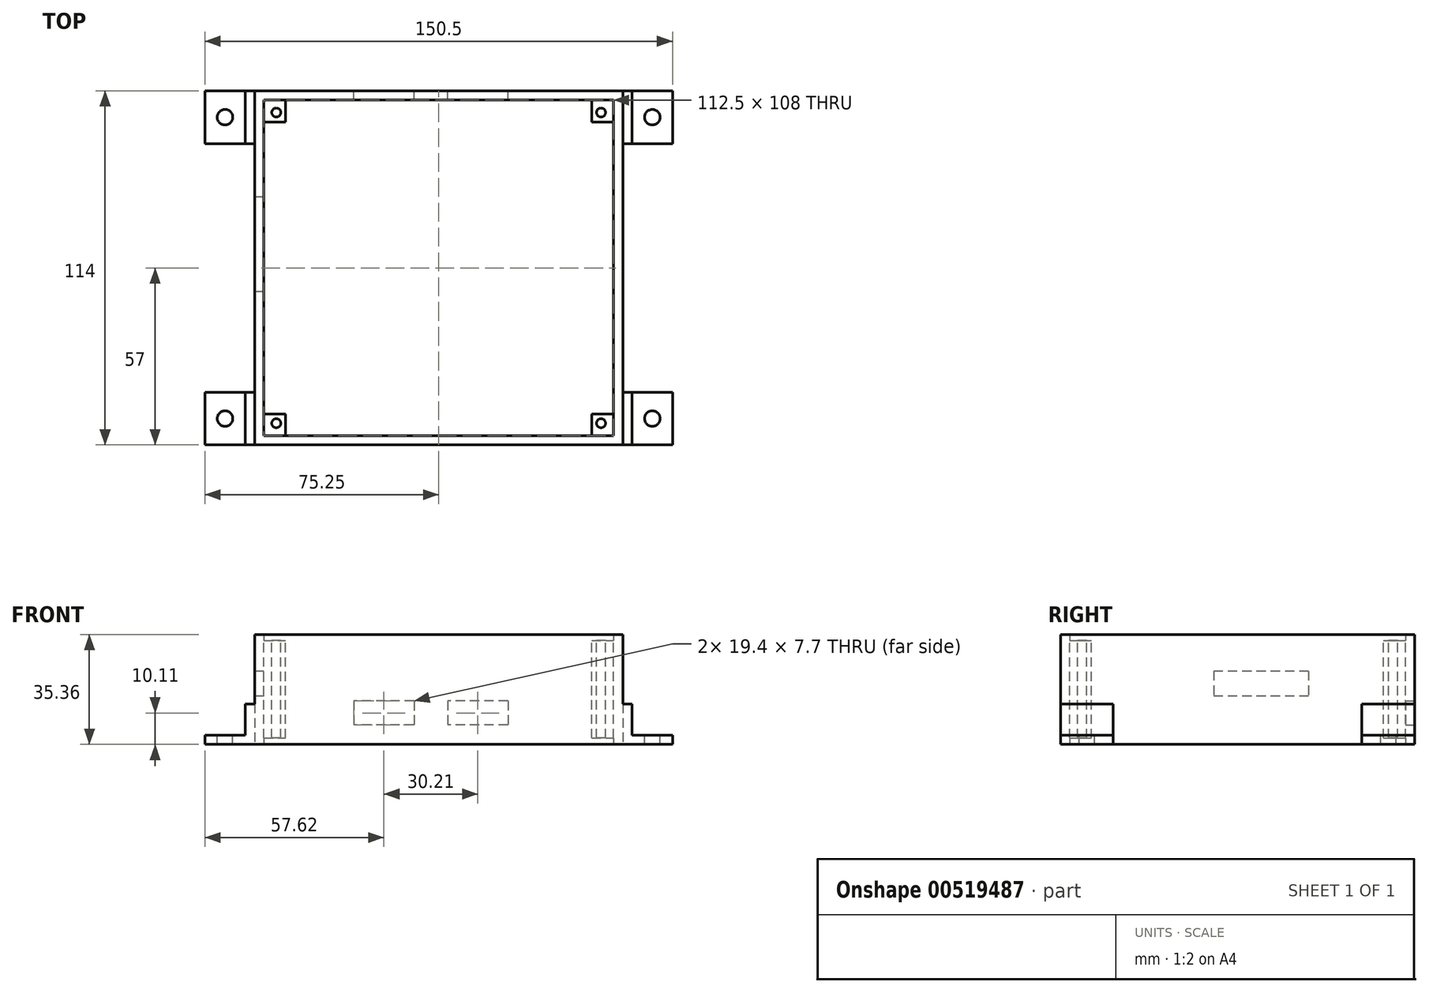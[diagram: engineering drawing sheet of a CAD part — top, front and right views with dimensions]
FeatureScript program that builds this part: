
annotation { "Feature Type Name" : "Feature", "Feature Type Description" : "" }
export const myFeature = defineFeature(function(context is Context, id is Id, definition is map)
    precondition{}
    {
        {
            var Q0;
            Q0=qCreatedBy(makeId("Top.planeOp"),FACE);
            var sketch = newSketch(context, id + "F0", { "sketchPlane" : qUnion([Q0])});
            skLineSegment(sketch, "E0.bottom", {"start": v(0, 0) * mm, "end": v(112.5, 0) * mm});
            skLineSegment(sketch, "E0.top", {"start": v(0, 108) * mm, "end": v(112.5, 108) * mm});
            skLineSegment(sketch, "E0.left", {"start": v(0, 0) * mm, "end": v(0, 108) * mm});
            skLineSegment(sketch, "E0.right", {"start": v(112.5, 0) * mm, "end": v(112.5, 108) * mm});
            skLineSegment(sketch, "E1.bottom", {"start": v(-3, -3) * mm, "end": v(115.5, -3) * mm});
            skLineSegment(sketch, "E1.top", {"start": v(-3, 111) * mm, "end": v(115.5, 111) * mm});
            skLineSegment(sketch, "E1.left", {"start": v(-3, -3) * mm, "end": v(-3, 111) * mm});
            skLineSegment(sketch, "E1.right", {"start": v(115.5, -3) * mm, "end": v(115.5, 111) * mm});
            skSolve(sketch);
        }
        {
            var Q0;
            Q0 = qSketchRegion(id + "F0", true);
            var Q1;
            Q1=makeQuery(id+"F0.imprint","IMPRINT",FACE,{"disambiguationData":[TD([[makeQuery(id+"F0.imprint","IMPRINT",EDGE,{"derivedFrom":sQuery(id+"F0.wireOp",EDGE,"5UW27vY8-DZkX-9mT5-oeWg-O9DarPSECfU4.bottom")}),-1.0]])]});
            var Q2;
            Q2=makeQuery(id+"F0.imprint","IMPRINT",FACE,{"disambiguationData":[TD([[makeQuery(id+"F0.imprint","IMPRINT",EDGE,{"derivedFrom":sQuery(id+"F0.wireOp",EDGE,"emjWjVMJ-dW8g-Ee0e-WItk-pn7yrFhIKDN6.bottom")}),1.0]])]});
            var Q3;
            Q3=makeQuery(id+"F0.imprint","IMPRINT",FACE,{"disambiguationData":[TD([[makeQuery(id+"F0.imprint","IMPRINT",EDGE,{"derivedFrom":sQuery(id+"F0.wireOp",EDGE,"Jp5ZSupj-YRPa-vJQM-HpLv-n2ZM76CLiCyT.bottom")}),1.0]])]});
            var Q4;
            Q4=makeQuery(id+"F0.imprint","IMPRINT",FACE,{"disambiguationData":[TD([[makeQuery(id+"F0.imprint","IMPRINT",EDGE,{"derivedFrom":sQuery(id+"F0.wireOp",EDGE,"ox3d0DqL-n6A3-UaFx-j0JZ-jM5fEP68q14y.bottom")}),-1.0]])]});
            extrude(context, id + "F1", {"entities" : qUnion([Q0, Q1, Q2, Q3, Q4]), "depth" : 35.36 * mm, "offsetDistance" : 25 * mm});
        }
        {
            var Q0;
            Q0=makeQuery(id+"F1.opExtrude","CAP_FACE",FACE,{"disambiguationData":[OSD([sQuery(id+"F0.wireOp",EDGE,"E0.bottom"),sQuery(id+"F0.wireOp",EDGE,"E0.top"),sQuery(id+"F0.wireOp",EDGE,"E0.left"),sQuery(id+"F0.wireOp",EDGE,"E0.right"),sQuery(id+"F0.wireOp",EDGE,"E1.bottom"),sQuery(id+"F0.wireOp",EDGE,"E1.top"),sQuery(id+"F0.wireOp",EDGE,"E1.left"),sQuery(id+"F0.wireOp",EDGE,"E1.right")])],"isStart":false});
            var sketch = newSketch(context, id + "F2", { "sketchPlane" : qUnion([Q0])});
            skLineSegment(sketch, "E2.bottom", {"start": v(0, 108) * mm, "end": v(7, 108) * mm});
            skLineSegment(sketch, "E2.top", {"start": v(0, 101) * mm, "end": v(7, 101) * mm});
            skLineSegment(sketch, "E2.left", {"start": v(0, 108) * mm, "end": v(0, 101) * mm});
            skLineSegment(sketch, "E2.right", {"start": v(7, 108) * mm, "end": v(7, 101) * mm});
            skLineSegment(sketch, "E3.bottom", {"start": v(112.5, 108) * mm, "end": v(105.5, 108) * mm});
            skLineSegment(sketch, "E3.top", {"start": v(112.5, 101) * mm, "end": v(105.5, 101) * mm});
            skLineSegment(sketch, "E3.left", {"start": v(112.5, 108) * mm, "end": v(112.5, 101) * mm});
            skLineSegment(sketch, "E3.right", {"start": v(105.5, 108) * mm, "end": v(105.5, 101) * mm});
            skLineSegment(sketch, "E4.bottom", {"start": v(112.5, 0) * mm, "end": v(105.5, 0) * mm});
            skLineSegment(sketch, "E4.top", {"start": v(112.5, 7) * mm, "end": v(105.5, 7) * mm});
            skLineSegment(sketch, "E4.left", {"start": v(112.5, 0) * mm, "end": v(112.5, 7) * mm});
            skLineSegment(sketch, "E4.right", {"start": v(105.5, 0) * mm, "end": v(105.5, 7) * mm});
            skLineSegment(sketch, "E5.bottom", {"start": v(0, 0) * mm, "end": v(7, 0) * mm});
            skLineSegment(sketch, "E5.top", {"start": v(0, 7) * mm, "end": v(7, 7) * mm});
            skLineSegment(sketch, "E5.left", {"start": v(0, 0) * mm, "end": v(0, 7) * mm});
            skLineSegment(sketch, "E5.right", {"start": v(7, 0) * mm, "end": v(7, 7) * mm});
            skSolve(sketch);
        }
        {
            var Q0;
            Q0=makeQuery(id+"F2.imprint","IMPRINT",FACE,{"disambiguationData":[TD([[makeQuery(id+"F2.imprint","IMPRINT",EDGE,{"derivedFrom":sQuery(id+"F2.wireOp",EDGE,"E2.bottom")}),-1.0]])]});
            var Q1;
            Q1=makeQuery(id+"F2.imprint","IMPRINT",FACE,{"disambiguationData":[TD([[makeQuery(id+"F2.imprint","IMPRINT",EDGE,{"derivedFrom":sQuery(id+"F2.wireOp",EDGE,"E3.bottom")}),-1.0]])]});
            var Q2;
            Q2=makeQuery(id+"F2.imprint","IMPRINT",FACE,{"disambiguationData":[TD([[makeQuery(id+"F2.imprint","IMPRINT",EDGE,{"derivedFrom":sQuery(id+"F2.wireOp",EDGE,"E4.bottom")}),1.0]])]});
            var Q3;
            Q3=makeQuery(id+"F2.imprint","IMPRINT",FACE,{"disambiguationData":[TD([[makeQuery(id+"F2.imprint","IMPRINT",EDGE,{"derivedFrom":sQuery(id+"F2.wireOp",EDGE,"E5.bottom")}),1.0]])]});
            extrude(context, id + "F3", {"entities" : qUnion([Q0, Q1, Q2, Q3]), "operationType" : NewBodyOperationType.ADD, "oppositeDirection" : true, "depth" : 33.36 * mm, "offsetDistance" : 25 * mm, "hasSecondDirection" : true, "secondDirectionOppositeDirection" : true, "secondDirectionDepth" : 2 * mm});
        }
        {
            var Q0;
            Q0=makeQuery(id+"F3.opExtrude","CAP_FACE",FACE,{"disambiguationData":[OSD([sQuery(id+"F2.wireOp",EDGE,"E2.bottom"),sQuery(id+"F2.wireOp",EDGE,"E2.top"),sQuery(id+"F2.wireOp",EDGE,"E2.left"),sQuery(id+"F2.wireOp",EDGE,"E2.right")])],"isStart":true});
            var sketch = newSketch(context, id + "F4", { "sketchPlane" : qUnion([Q0])});
            skCircle(sketch, "E6", {"center": v(4, 104) * mm, "radius": 1.45 * mm});
            skCircle(sketch, "E7", {"center": v(108.5, 104) * mm, "radius": 1.45 * mm});
            skCircle(sketch, "E8", {"center": v(4, 4) * mm, "radius": 1.45 * mm});
            skCircle(sketch, "E9", {"center": v(108.5, 4) * mm, "radius": 1.45 * mm});
            skSolve(sketch);
        }
        {
            var Q0;
            Q0=makeQuery(id+"F4.imprint","IMPRINT",FACE,{"disambiguationData":[TD([[makeQuery(id+"F4.imprint","IMPRINT",EDGE,{"derivedFrom":sQuery(id+"F4.wireOp",EDGE,"E6")}),1.0]])]});
            var Q1;
            Q1=makeQuery(id+"F4.imprint","IMPRINT",FACE,{"disambiguationData":[TD([[makeQuery(id+"F4.imprint","IMPRINT",EDGE,{"derivedFrom":sQuery(id+"F4.wireOp",EDGE,"E7")}),1.0]])]});
            var Q2;
            Q2=makeQuery(id+"F4.imprint","IMPRINT",FACE,{"disambiguationData":[TD([[makeQuery(id+"F4.imprint","IMPRINT",EDGE,{"derivedFrom":sQuery(id+"F4.wireOp",EDGE,"E8")}),1.0]])]});
            var Q3;
            Q3=makeQuery(id+"F4.imprint","IMPRINT",FACE,{"disambiguationData":[TD([[makeQuery(id+"F4.imprint","IMPRINT",EDGE,{"derivedFrom":sQuery(id+"F4.wireOp",EDGE,"E9")}),1.0]])]});
            extrude(context, id + "F5", {"entities" : qUnion([Q0, Q1, Q2, Q3]), "operationType" : NewBodyOperationType.REMOVE, "endBound" : BoundingType.THROUGH_ALL, "oppositeDirection" : true, "depth" : 25 * mm, "offsetDistance" : 25 * mm});
        }
        {
            var Q0;
            Q0=makeQuery(id+"F1.opExtrude","SWEPT_FACE",FACE,{"disambiguationData":[OSD([sQuery(id+"F0.wireOp",EDGE,"E1.left")])]});
            var sketch = newSketch(context, id + "F6", { "sketchPlane" : qUnion([Q0])});
            skLineSegment(sketch, "E10.bottom", {"start": v(-76.87, 23.54) * mm, "end": v(-46.36, 23.54) * mm});
            skLineSegment(sketch, "E10.top", {"start": v(-76.87, 15.54) * mm, "end": v(-46.36, 15.54) * mm});
            skLineSegment(sketch, "E10.left", {"start": v(-76.87, 23.54) * mm, "end": v(-76.87, 15.54) * mm});
            skLineSegment(sketch, "E10.right", {"start": v(-46.36, 23.54) * mm, "end": v(-46.36, 15.54) * mm});
            skSolve(sketch);
        }
        {
            var Q0;
            Q0=makeQuery(id+"F6.imprint","IMPRINT",FACE,{"disambiguationData":[TD([[makeQuery(id+"F6.imprint","IMPRINT",EDGE,{"derivedFrom":sQuery(id+"F6.wireOp",EDGE,"E10.bottom")}),-1.0]])]});
            extrude(context, id + "F7", {"entities" : qUnion([Q0]), "operationType" : NewBodyOperationType.REMOVE, "endBound" : BoundingType.UP_TO_NEXT, "oppositeDirection" : true, "depth" : 3 * mm, "offsetDistance" : 25 * mm});
        }
        {
            var Q0;
            Q0=makeQuery(id+"F1.opExtrude","SWEPT_FACE",FACE,{"disambiguationData":[OSD([sQuery(id+"F0.wireOp",EDGE,"E1.top")])]});
            var sketch = newSketch(context, id + "F8", { "sketchPlane" : qUnion([Q0])});
            skLineSegment(sketch, "E11.bottom", {"start": v(-48.32, 13.96) * mm, "end": v(-28.92, 13.96) * mm});
            skLineSegment(sketch, "E11.top", {"start": v(-48.32, 6.26) * mm, "end": v(-28.92, 6.26) * mm});
            skLineSegment(sketch, "E11.left", {"start": v(-48.32, 13.96) * mm, "end": v(-48.32, 6.26) * mm});
            skLineSegment(sketch, "E11.right", {"start": v(-28.92, 13.96) * mm, "end": v(-28.92, 6.26) * mm});
            skLineSegment(sketch, "E12.bottom", {"start": v(-78.53, 13.96) * mm, "end": v(-59.13, 13.96) * mm});
            skLineSegment(sketch, "E12.top", {"start": v(-78.53, 6.26) * mm, "end": v(-59.13, 6.26) * mm});
            skLineSegment(sketch, "E12.left", {"start": v(-78.53, 13.96) * mm, "end": v(-78.53, 6.26) * mm});
            skLineSegment(sketch, "E12.right", {"start": v(-59.13, 13.96) * mm, "end": v(-59.13, 6.26) * mm});
            skSolve(sketch);
        }
        {
            var Q0;
            Q0=makeQuery(id+"F8.imprint","IMPRINT",FACE,{"disambiguationData":[TD([[makeQuery(id+"F8.imprint","IMPRINT",EDGE,{"derivedFrom":sQuery(id+"F8.wireOp",EDGE,"E12.bottom")}),-1.0]])]});
            var Q1;
            Q1=makeQuery(id+"F8.imprint","IMPRINT",FACE,{"disambiguationData":[TD([[makeQuery(id+"F8.imprint","IMPRINT",EDGE,{"derivedFrom":sQuery(id+"F8.wireOp",EDGE,"E11.bottom")}),-1.0]])]});
            extrude(context, id + "F9", {"entities" : qUnion([Q0, Q1]), "operationType" : NewBodyOperationType.REMOVE, "oppositeDirection" : true, "depth" : 3 * mm, "offsetDistance" : 25 * mm});
        }
        {
            var Q0;
            Q0=makeQuery(id+"F1.opExtrude","SWEPT_FACE",FACE,{"disambiguationData":[OSD([sQuery(id+"F0.wireOp",EDGE,"E1.bottom")])]});
            var sketch = newSketch(context, id + "F10", { "sketchPlane" : qUnion([Q0])});
            skLineSegment(sketch, "E13", {"start": v(-19, 3) * mm, "end": v(-6, 3) * mm});
            skLineSegment(sketch, "E14", {"start": v(-6, 3) * mm, "end": v(-6, 13) * mm});
            skLineSegment(sketch, "E15", {"start": v(-6, 13) * mm, "end": v(-3, 13) * mm});
            skLineSegment(sketch, "E16", {"start": v(-19, 3) * mm, "end": v(-19, 0) * mm});
            skLineSegment(sketch, "E17", {"start": v(-19, 0) * mm, "end": v(-3, 0) * mm});
            skLineSegment(sketch, "E18", {"start": v(-3, 13) * mm, "end": v(-3, 0) * mm});
            skSolve(sketch);
        }
        {
            var Q0;
            Q0=makeQuery(id+"F10.imprint","IMPRINT",FACE,{"disambiguationData":[TD([[makeQuery(id+"F10.imprint","IMPRINT",EDGE,{"derivedFrom":sQuery(id+"F10.wireOp",EDGE,"E13")}),-1.0]])]});
            extrude(context, id + "F11", {"entities" : qUnion([Q0]), "operationType" : NewBodyOperationType.ADD, "oppositeDirection" : true, "depth" : 114 * mm, "offsetDistance" : 25 * mm});
        }
        {
            var Q0;
            Q0=makeQuery(id+"F11.boolean.opBoolean","MERGE",FACE,{"derivedFrom":[makeQuery(id+"F1.opExtrude","SWEPT_FACE",FACE,{"disambiguationData":[OSD([sQuery(id+"F0.wireOp",EDGE,"E1.bottom")])]}),makeQuery(id+"F11.opExtrude","CAP_FACE",FACE,{"disambiguationData":[OSD([sQuery(id+"F10.wireOp",EDGE,"E13"),sQuery(id+"F10.wireOp",EDGE,"E14"),sQuery(id+"F10.wireOp",EDGE,"E15"),sQuery(id+"F10.wireOp",EDGE,"E16"),sQuery(id+"F10.wireOp",EDGE,"E17"),sQuery(id+"F10.wireOp",EDGE,"E18")])],"isStart":true})]});
            var sketch = newSketch(context, id + "F12", { "sketchPlane" : qUnion([Q0])});
            skLineSegment(sketch, "E19", {"start": v(115.5, 13) * mm, "end": v(115.5, 0) * mm});
            skLineSegment(sketch, "E20", {"start": v(115.5, 0) * mm, "end": v(131.5, 0) * mm});
            skLineSegment(sketch, "E21", {"start": v(131.5, 0) * mm, "end": v(131.5, 3) * mm});
            skLineSegment(sketch, "E22", {"start": v(131.5, 3) * mm, "end": v(118.5, 3) * mm});
            skLineSegment(sketch, "E23", {"start": v(118.5, 3) * mm, "end": v(118.5, 13) * mm});
            skLineSegment(sketch, "E24", {"start": v(118.5, 13) * mm, "end": v(115.5, 13) * mm});
            skSolve(sketch);
        }
        {
            var Q0;
            Q0=makeQuery(id+"F12.imprint","IMPRINT",FACE,{"disambiguationData":[TD([[makeQuery(id+"F12.imprint","IMPRINT",EDGE,{"derivedFrom":sQuery(id+"F12.wireOp",EDGE,"E19")}),1.0]])]});
            extrude(context, id + "F13", {"entities" : qUnion([Q0]), "operationType" : NewBodyOperationType.ADD, "oppositeDirection" : true, "depth" : 114 * mm, "offsetDistance" : 25 * mm});
        }
        {
            var Q0;
            Q0=makeQuery(id+"F13.boolean.opBoolean","MERGE",FACE,{"derivedFrom":[makeQuery(id+"F11.boolean.opBoolean","MERGE",FACE,{"derivedFrom":[makeQuery(id+"F1.opExtrude","CAP_FACE",FACE,{"disambiguationData":[OSD([sQuery(id+"F0.wireOp",EDGE,"E0.bottom"),sQuery(id+"F0.wireOp",EDGE,"E0.top"),sQuery(id+"F0.wireOp",EDGE,"E0.left"),sQuery(id+"F0.wireOp",EDGE,"E0.right"),sQuery(id+"F0.wireOp",EDGE,"E1.bottom"),sQuery(id+"F0.wireOp",EDGE,"E1.top"),sQuery(id+"F0.wireOp",EDGE,"E1.left"),sQuery(id+"F0.wireOp",EDGE,"E1.right")])],"isStart":true}),makeQuery(id+"F11.opExtrude","SWEPT_FACE",FACE,{"disambiguationData":[OSD([sQuery(id+"F10.wireOp",EDGE,"E17")])]})]}),makeQuery(id+"F13.opExtrude","SWEPT_FACE",FACE,{"disambiguationData":[OSD([sQuery(id+"F12.wireOp",EDGE,"E20")])]})]});
            var sketch = newSketch(context, id + "F14", { "sketchPlane" : qUnion([Q0])});
            skSolve(sketch);
        }
        {
            var Q0;
            Q0=makeQuery(id+"F14.imprint","IMPRINT",FACE,{"disambiguationData":[TD([[makeQuery(id+"F14.imprint","IMPRINT",EDGE,{"derivedFrom":makeQuery(id+"F1.opExtrude","CAP_EDGE",EDGE,{"disambiguationData":[OSD([sQuery(id+"F0.wireOp",EDGE,"E0.bottom")])],"isStart":true})}),1.0]])]});
            var sketch = newSketch(context, id + "F15", { "sketchPlane" : qUnion([Q0])});
            skLineSegment(sketch, "E25.bottom", {"start": v(-19, -14) * mm, "end": v(-3, -14) * mm});
            skLineSegment(sketch, "E25.top", {"start": v(-19, -94) * mm, "end": v(-3, -94) * mm});
            skLineSegment(sketch, "E25.left", {"start": v(-19, -14) * mm, "end": v(-19, -94) * mm});
            skLineSegment(sketch, "E25.right", {"start": v(-3, -14) * mm, "end": v(-3, -94) * mm});
            skSolve(sketch);
        }
        {
            var Q0;
            Q0 = qSketchRegion(id + "F15", true);
            extrude(context, id + "F16", {"entities" : qUnion([Q0]), "operationType" : NewBodyOperationType.REMOVE, "endBound" : BoundingType.THROUGH_ALL, "oppositeDirection" : true, "depth" : 25 * mm, "offsetDistance" : 25 * mm});
        }
        {
            var Q0;
            Q0=makeQuery(id+"F14.imprint","IMPRINT",FACE,{"disambiguationData":[TD([[makeQuery(id+"F14.imprint","IMPRINT",EDGE,{"derivedFrom":makeQuery(id+"F1.opExtrude","CAP_EDGE",EDGE,{"disambiguationData":[OSD([sQuery(id+"F0.wireOp",EDGE,"E0.bottom")])],"isStart":true})}),1.0]])]});
            var sketch = newSketch(context, id + "F17", { "sketchPlane" : qUnion([Q0])});
            skLineSegment(sketch, "E26.bottom", {"start": v(115.5, -14) * mm, "end": v(131.5, -14) * mm});
            skLineSegment(sketch, "E26.top", {"start": v(115.5, -94) * mm, "end": v(131.5, -94) * mm});
            skLineSegment(sketch, "E26.left", {"start": v(115.5, -14) * mm, "end": v(115.5, -94) * mm});
            skLineSegment(sketch, "E26.right", {"start": v(131.5, -14) * mm, "end": v(131.5, -94) * mm});
            skSolve(sketch);
        }
        {
            var Q0;
            Q0 = qSketchRegion(id + "F17", true);
            extrude(context, id + "F18", {"entities" : qUnion([Q0]), "operationType" : NewBodyOperationType.REMOVE, "endBound" : BoundingType.THROUGH_ALL, "oppositeDirection" : true, "depth" : 25 * mm, "offsetDistance" : 25 * mm});
        }
        {
            var Q0;
            {var subQ2=sQuery(id+"F10.wireOp",EDGE,"E13");Q0=makeQuery(id+"F16.boolean.opBoolean","SPLIT",FACE,{"disambiguationData":[TD([makeQuery(id+"F1.opExtrude","SWEPT_FACE",FACE,{"disambiguationData":[OSD([sQuery(id+"F0.wireOp",EDGE,"E1.top")])]})])],"derivedFrom":makeQuery(id+"F11.opExtrude","SWEPT_FACE",FACE,{"disambiguationData":[OSD([subQ2])]})});}
            var sketch = newSketch(context, id + "F19", { "sketchPlane" : qUnion([Q0])});
            skCircle(sketch, "E27", {"center": v(-12.5, 102.5) * mm, "radius": 2.5 * mm});
            skCircle(sketch, "E28", {"center": v(125, 102.5) * mm, "radius": 2.5 * mm});
            skCircle(sketch, "E29", {"center": v(125, 5.5) * mm, "radius": 2.5 * mm});
            skCircle(sketch, "E30", {"center": v(-12.5, 5.5) * mm, "radius": 2.5 * mm});
            skSolve(sketch);
        }
        {
            var Q0;
            Q0=makeQuery(id+"F19.imprint","IMPRINT",FACE,{"disambiguationData":[TD([[makeQuery(id+"F19.imprint","IMPRINT",EDGE,{"derivedFrom":sQuery(id+"F19.wireOp",EDGE,"E27")}),1.0]])]});
            var Q1;
            Q1=makeQuery(id+"F19.imprint","IMPRINT",FACE,{"disambiguationData":[TD([[makeQuery(id+"F19.imprint","IMPRINT",EDGE,{"derivedFrom":sQuery(id+"F19.wireOp",EDGE,"E28")}),1.0]])]});
            var Q2;
            Q2=makeQuery(id+"F19.imprint","IMPRINT",FACE,{"disambiguationData":[TD([[makeQuery(id+"F19.imprint","IMPRINT",EDGE,{"derivedFrom":sQuery(id+"F19.wireOp",EDGE,"E29")}),1.0]])]});
            var Q3;
            Q3=makeQuery(id+"F19.imprint","IMPRINT",FACE,{"disambiguationData":[TD([[makeQuery(id+"F19.imprint","IMPRINT",EDGE,{"derivedFrom":sQuery(id+"F19.wireOp",EDGE,"E30")}),1.0]])]});
            extrude(context, id + "F20", {"entities" : qUnion([Q0, Q1, Q2, Q3]), "operationType" : NewBodyOperationType.REMOVE, "endBound" : BoundingType.THROUGH_ALL, "oppositeDirection" : true, "depth" : 25 * mm, "offsetDistance" : 25 * mm});
        }
    });
